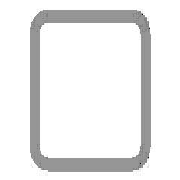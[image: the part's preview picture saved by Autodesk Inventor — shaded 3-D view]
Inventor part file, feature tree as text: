
AUTODESK INVENTOR PART (.ipt)
format: ipt  version: 2023 (Build 270158000, 158)  size: 199,680 bytes
history: native  units: mm (DEFAULTED — no unit token found)
features: other x14, sketch x5, extrude x3, plane x1
ambient origin geometry x8: Origin, YZ Plane, XZ Plane, XY Plane, X Axis, Y Axis, Z Axis, Center Point
bodies: Solid1 (feature_tree)
feature tree (23):
  parser-record x1  (decoder bookkeeping rows leaked as tree rows — omitted from the tree; the rows remain in map.json)
  other  "Driven Length"
  other  "Płaszczyzna początkowa"
  other  "Płaszczyzna końcowa"
  extrude  "Bryła"  TaperAngle=0.0deg  [1 undecoded]
  other  "Płaszczyzna konstrukcyjna4"
  other  "Płaszczyzna konstrukcyjna5"
  other  "Płaszczyzna konstrukcyjna6"
  extrude  "Wyciągnięcie proste2"  Depth=1500.0mm
  other  "Utwórz kombinację1"
  other  "Płaszczyzna konstrukcyjna7"
  other  "Płaszczyzna konstrukcyjna8"
  other  "Płaszczyzna konstrukcyjna9"
  extrude  "Wyciągnięcie proste3"  Depth=1500.0mm
  other  "Utwórz kombinację2"
  sketch  "Szkic"
  sketch  "Sketch3"  dims[d3=1500.0mm d4=0.0mm]
  plane  "Work Plane3"
  sketch  "Sketch4"  dims[d7=4.0mm d10=40.0mm d11=40.0mm d12=3.2mm d13=-0.0mm d14=1500.0mm d15=20.0mm d16=20.0mm d17=90.0deg d18=1500.0mm d19=0.13mm d20=0.0mm d21=0.13mm d22=0.0mm]
  sketch  "Szkic5"
  other  "Bryła2"
  sketch  "Szkic6"
  other  "Bryła3"
note: 1 required parameter value undecoded (feature->parameter linkage not recoverable at this tier; creation-order binding heuristic only, values carry confidence <= 0.55)
